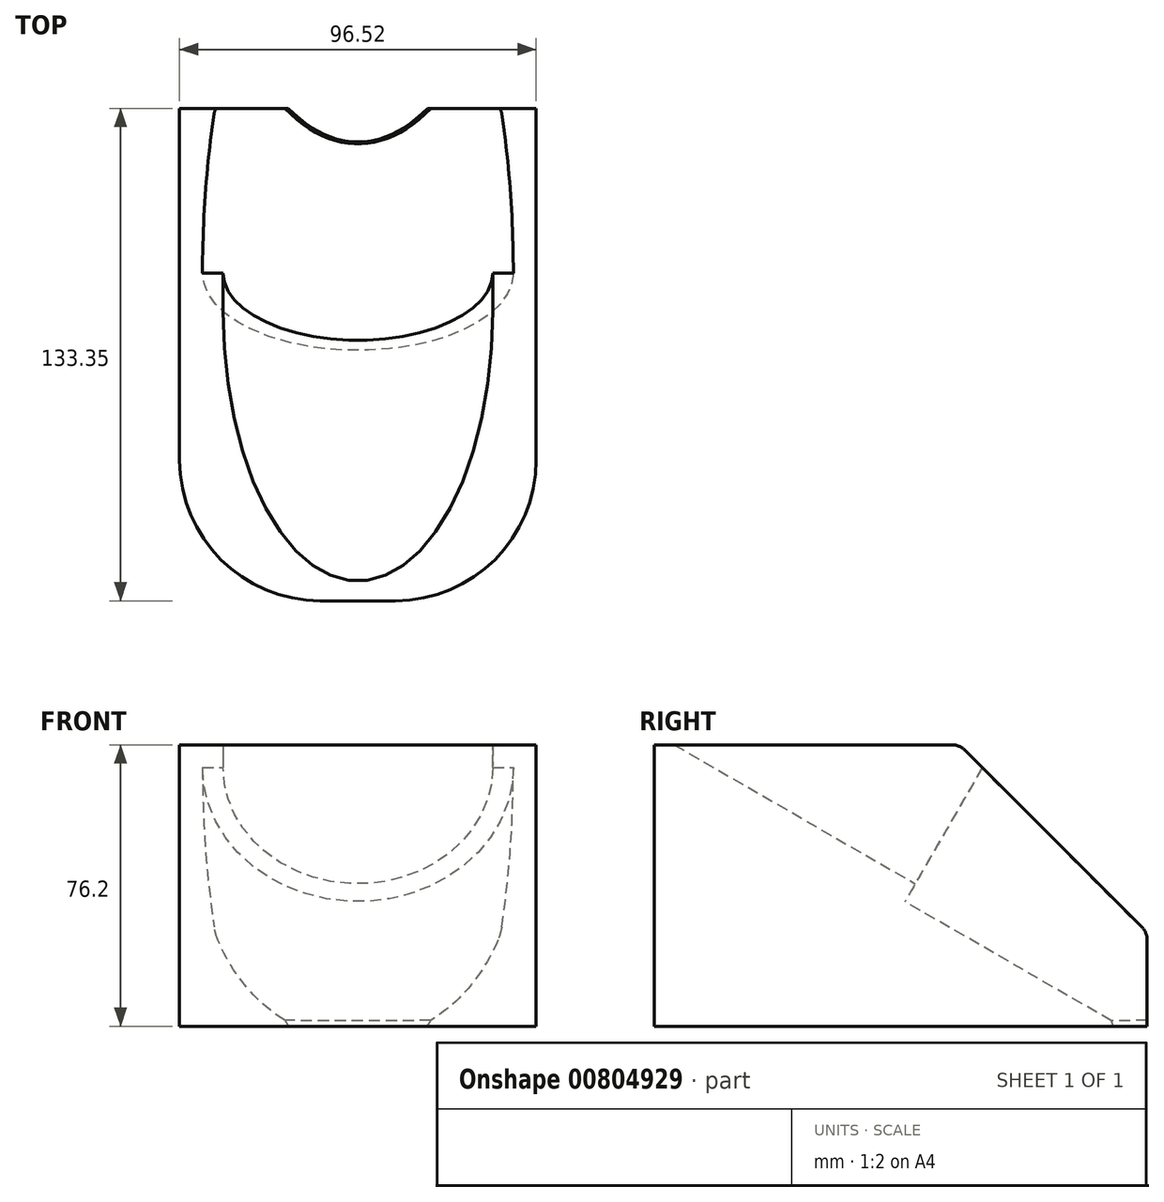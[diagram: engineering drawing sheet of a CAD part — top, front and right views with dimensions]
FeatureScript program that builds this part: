
annotation { "Feature Type Name" : "Feature", "Feature Type Description" : "" }
export const myFeature = defineFeature(function(context is Context, id is Id, definition is map)
    precondition{}
    {
        {
            var Q0;
            Q0=qCreatedBy(makeId("Top.planeOp"),FACE);
            var sketch = newSketch(context, id + "F0", { "sketchPlane" : qUnion([Q0])});
            skLineSegment(sketch, "E0.bottom", {"start": v(-96.52, 133.35) * mm, "end": v(0, 133.35) * mm});
            skLineSegment(sketch, "E0.top", {"start": v(-96.52, 0) * mm, "end": v(0, 0) * mm});
            skLineSegment(sketch, "E0.left", {"start": v(-96.52, 133.35) * mm, "end": v(-96.52, 0) * mm});
            skLineSegment(sketch, "E0.right", {"start": v(0, 133.35) * mm, "end": v(0, 0) * mm});
            skSolve(sketch);
        }
        {
            var Q0;
            Q0 = qSketchRegion(id + "F0", true);
            extrude(context, id + "F1", {"entities" : qUnion([Q0]), "depth" : 76.2 * mm, "offsetDistance" : 25.4 * mm});
        }
        {
            var Q0;
            Q0=makeQuery(id+"F1.opExtrude","CAP_EDGE",EDGE,{"disambiguationData":[OSD([sQuery(id+"F0.wireOp",EDGE,"E0.bottom")])],"isStart":true});
            cPlane(context, id + "F2", {"entities" : qUnion([Q0]), "cplaneType" : CPlaneType.LINE_ANGLE, "offset" : 25.4 * mm, "angle" : -30 * degree, "width" : 152.4 * mm, "height" : 152.4 * mm});
        }
        {
            var Q0;
            Q0=qCreatedBy(id+"F2.planeOp",FACE);
            var sketch = newSketch(context, id + "F3", { "sketchPlane" : qUnion([Q0])});
            skArc(sketch, "E1", {"start": v(11.75, 105.19) * mm, "mid": v(48.26, 68.68) * mm, "end": v(84.77, 105.19) * mm});
            skPoint(sketch, "E2", {"position": v(48.26, 66.68) * mm});
            skLineSegment(sketch, "E3", {"start": v(48.26, 66.68) * mm, "end": v(48.26, 105.19) * mm, "construction": true});
            skLineSegment(sketch, "E4", {"start": v(84.77, 105.19) * mm, "end": v(84.77, 175.6) * mm});
            skLineSegment(sketch, "E5", {"start": v(84.77, 175.6) * mm, "end": v(11.75, 175.6) * mm});
            skLineSegment(sketch, "E6", {"start": v(11.75, 175.6) * mm, "end": v(11.75, 105.19) * mm});
            skSolve(sketch);
        }
        {
            var Q0;
            Q0 = qSketchRegion(id + "F3", true);
            extrude(context, id + "F4", {"entities" : qUnion([Q0]), "operationType" : NewBodyOperationType.REMOVE, "endBound" : BoundingType.THROUGH_ALL, "oppositeDirection" : true, "depth" : 25.4 * mm, "offsetDistance" : 25.4 * mm});
        }
        {
            var Q0;
            {var subQ0=sQuery(id+"F0.wireOp",EDGE,"E0.bottom");var subQ1=sQuery(id+"F0.wireOp",EDGE,"E0.right");Q0=makeQuery(id+"F4.boolean.opBoolean","SPLIT",EDGE,{"disambiguationData":[TD([makeQuery(id+"F1.opExtrude","SWEPT_FACE",FACE,{"disambiguationData":[OSD([subQ1])]})])],"derivedFrom":makeQuery(id+"F1.opExtrude","CAP_EDGE",EDGE,{"disambiguationData":[OSD([subQ0])],"isStart":false})});}
            var Q1;
            {var subQ0=sQuery(id+"F0.wireOp",EDGE,"E0.bottom");var subQ1=sQuery(id+"F0.wireOp",EDGE,"E0.left");Q1=makeQuery(id+"F4.boolean.opBoolean","SPLIT",EDGE,{"disambiguationData":[TD([makeQuery(id+"F1.opExtrude","SWEPT_FACE",FACE,{"disambiguationData":[OSD([subQ1])]})])],"derivedFrom":makeQuery(id+"F1.opExtrude","CAP_EDGE",EDGE,{"disambiguationData":[OSD([subQ0])],"isStart":false})});}
            chamfer(context, id + "F5", {"entities" : qUnion([Q0, Q1]), "width" : 50.8 * mm, "tangentPropagation" : true});
        }
        {
            var Q0;
            Q0=qCreatedBy(id+"F2.planeOp",FACE);
            cPlane(context, id + "F6", {"entities" : qUnion([Q0]), "cplaneType" : CPlaneType.OFFSET, "offset" : 73.66 * mm, "oppositeDirection" : true, "width" : 152.4 * mm, "height" : 152.4 * mm});
        }
        {
            var Q0;
            Q0=qCreatedBy(id+"F6.planeOp",FACE);
            var sketch = newSketch(context, id + "F7", { "sketchPlane" : qUnion([Q0])});
            skCircle(sketch, "E7", {"center": v(48.26, 105.19) * mm, "radius": 42.07 * mm});
            skSolve(sketch);
        }
        {
            var Q0;
            Q0 = qSketchRegion(id + "F7", true);
            extrude(context, id + "F8", {"entities" : qUnion([Q0]), "operationType" : NewBodyOperationType.REMOVE, "endBound" : BoundingType.THROUGH_ALL, "depth" : 25.4 * mm, "offsetDistance" : 25.4 * mm});
        }
        {
            var Q0;
            Q0=makeQuery(id+"F8.boolean.opBoolean","INTERSECT",EDGE,{"derivedFrom":[makeQuery(id+"F1.opExtrude","CAP_FACE",FACE,{"disambiguationData":[OSD([sQuery(id+"F0.wireOp",EDGE,"E0.bottom"),sQuery(id+"F0.wireOp",EDGE,"E0.top"),sQuery(id+"F0.wireOp",EDGE,"E0.left"),sQuery(id+"F0.wireOp",EDGE,"E0.right")])],"isStart":true}),makeQuery(id+"F8.opExtrude","SWEPT_FACE",FACE,{"disambiguationData":[OSD([sQuery(id+"F7.wireOp",EDGE,"E7")])]})]});
            chamfer(context, id + "F9", {"entities" : qUnion([Q0]), "chamferType" : ChamferType.OFFSET_ANGLE, "width" : 2.54 * mm, "oppositeDirection" : false, "angle" : 30 * degree, "tangentPropagation" : true});
        }
        {
            var Q0;
            {var subQ0=sQuery(id+"F0.wireOp",EDGE,"E0.bottom");var subQ1=makeQuery(id+"F1.opExtrude","SWEPT_FACE",FACE,{"disambiguationData":[OSD([subQ0])]});var subQ2=sQuery(id+"F0.wireOp",EDGE,"E0.left");Q0=makeQuery(id+"F5.opChamfer","BLEND_EDGE",EDGE,{"blendedFrom":[makeQuery(id+"F4.boolean.opBoolean","SPLIT",EDGE,{"disambiguationData":[TD([makeQuery(id+"F1.opExtrude","SWEPT_FACE",FACE,{"disambiguationData":[OSD([subQ2])]})])],"derivedFrom":makeQuery(id+"F1.opExtrude","CAP_EDGE",EDGE,{"disambiguationData":[OSD([subQ0])],"isStart":false})}),subQ1],"blendedInto":[subQ1]});}
            var Q1;
            {var subQ0=sQuery(id+"F0.wireOp",EDGE,"E0.bottom");var subQ1=makeQuery(id+"F1.opExtrude","SWEPT_FACE",FACE,{"disambiguationData":[OSD([subQ0])]});var subQ2=sQuery(id+"F0.wireOp",EDGE,"E0.right");Q1=makeQuery(id+"F5.opChamfer","BLEND_EDGE",EDGE,{"blendedFrom":[makeQuery(id+"F4.boolean.opBoolean","SPLIT",EDGE,{"disambiguationData":[TD([makeQuery(id+"F1.opExtrude","SWEPT_FACE",FACE,{"disambiguationData":[OSD([subQ2])]})])],"derivedFrom":makeQuery(id+"F1.opExtrude","CAP_EDGE",EDGE,{"disambiguationData":[OSD([subQ0])],"isStart":false})}),subQ1],"blendedInto":[subQ1]});}
            fillet(context, id + "F10", {"entities" : qUnion([Q0, Q1]), "tangentPropagation" : true, "radius" : 5.08 * mm, "defaultsChanged" : false, "vertexSettings" : [], "allowEdgeOverflow" : false});
        }
        {
            var Q0;
            Q0=makeQuery(id+"F1.opExtrude","SWEPT_EDGE",EDGE,{"disambiguationData":[OSD([sQuery(id+"F0.wireOp",EDGE,"E0.top"),sQuery(id+"F0.wireOp",EDGE,"E0.left")])]});
            var Q1;
            Q1=makeQuery(id+"F1.opExtrude","SWEPT_EDGE",EDGE,{"disambiguationData":[OSD([sQuery(id+"F0.wireOp",EDGE,"E0.top"),sQuery(id+"F0.wireOp",EDGE,"E0.right")])]});
            fillet(context, id + "F11", {"entities" : qUnion([Q0, Q1]), "tangentPropagation" : true, "radius" : 38.1 * mm, "defaultsChanged" : true, "vertexSettings" : [], "allowEdgeOverflow" : false});
        }
        {
            var Q0;
            {var subQ0=sQuery(id+"F0.wireOp",EDGE,"E0.right");var subQ1=sQuery(id+"F0.wireOp",EDGE,"E0.bottom");var subQ2=makeQuery(id+"F1.opExtrude","CAP_FACE",FACE,{"disambiguationData":[OSD([subQ1,sQuery(id+"F0.wireOp",EDGE,"E0.top"),sQuery(id+"F0.wireOp",EDGE,"E0.left"),subQ0])],"isStart":false});Q0=makeQuery(id+"F5.opChamfer","BLEND_EDGE",EDGE,{"blendedFrom":[makeQuery(id+"F4.boolean.opBoolean","SPLIT",EDGE,{"disambiguationData":[TD([makeQuery(id+"F1.opExtrude","SWEPT_FACE",FACE,{"disambiguationData":[OSD([subQ0])]})])],"derivedFrom":makeQuery(id+"F1.opExtrude","CAP_EDGE",EDGE,{"disambiguationData":[OSD([subQ1])],"isStart":false})}),subQ2],"blendedInto":[subQ2]});}
            var Q1;
            {var subQ0=sQuery(id+"F0.wireOp",EDGE,"E0.left");var subQ1=sQuery(id+"F0.wireOp",EDGE,"E0.bottom");var subQ2=makeQuery(id+"F1.opExtrude","CAP_FACE",FACE,{"disambiguationData":[OSD([subQ1,sQuery(id+"F0.wireOp",EDGE,"E0.top"),subQ0,sQuery(id+"F0.wireOp",EDGE,"E0.right")])],"isStart":false});Q1=makeQuery(id+"F5.opChamfer","BLEND_EDGE",EDGE,{"blendedFrom":[makeQuery(id+"F4.boolean.opBoolean","SPLIT",EDGE,{"disambiguationData":[TD([makeQuery(id+"F1.opExtrude","SWEPT_FACE",FACE,{"disambiguationData":[OSD([subQ0])]})])],"derivedFrom":makeQuery(id+"F1.opExtrude","CAP_EDGE",EDGE,{"disambiguationData":[OSD([subQ1])],"isStart":false})}),subQ2],"blendedInto":[subQ2]});}
            fillet(context, id + "F12", {"entities" : qUnion([Q0, Q1]), "tangentPropagation" : true, "radius" : 5.08 * mm, "defaultsChanged" : false, "vertexSettings" : [], "allowEdgeOverflow" : false});
        }
    });
